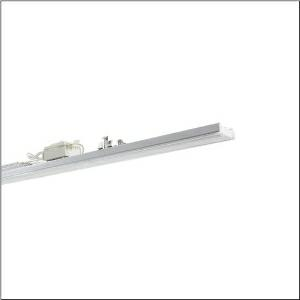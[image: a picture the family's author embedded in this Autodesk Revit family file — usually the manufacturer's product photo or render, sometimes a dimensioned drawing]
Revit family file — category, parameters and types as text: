
# Revit family: licross_r__11_recessed_mo_51te18dn495g_1a16
name_source: partatom
category: Lighting Fixtures
units: mm (PartAtom-declared; Revit-internal decimal feet)

## family parameters
Cut with Voids When Loaded = No
Host = Face
Light Source = No
Part Type = Normal
Room Calculation Point = No
Round Connector Dimension = Use Diameter
Shared = No

## types (1)
- --- (1 x LED, 9950 lm, 56.7 W, 4000K)
    Apparent Load = 57 VA
    CIE Flux Codes = 83 96 99 100 100
    Color Rendering = 80
    Color Temperature = 4000K
    Default Elevation = 1800 mm
    Description = Licross® 11 Recessed MO, luminaire insert, of sheet steel, galvanised, coil coated, white, length: 1.500mm, width: 66mm, height: 67mm, LED rated luminous flux: 9.950lm, light colour: 840, control gear: DALI 2, with plug, 5-pole, with phase selection, mains connection: 220..240V, AC, 50/60Hz, rated input power: 57W, halogen-free wiring, primary light control with lens, of plastic, primary optical cover: cover, of PMMA, light emission: direct distribution, primary light characteristic: symmetric, protection rating (complete): IP54, insulation class (complete): insulation class I (protective earthing), certification: CE, ENEC, VDE, UKCA, protection symbol: D if used in an environment with non-conductive dust loads with corresponding accessories, impact resistance: IK06, permissible ambient temperature for indoor applications: -25..+35°C, corresponds to IFS (International Featured Standards) requirements for safety and quality in the food industry, reducing of maximum allowable ambient temperature of 5°C with ceiling mounting, LABS conformity tested according to VDMA 24364:2018-05, packaging unit: 1 piece
    Height = 58 mm
    Lamp = 1 x LED
    Lamp Light Flux = 9950 lm
    Lamp Power = 56.7 W
    Lamp count = 1
    Length = 1500 mm
    Luminous efficacy = 175 lm/W
    Manufacturer = Siteco
    ModVariant = No
    Model = 51TE18DN495G
    Mounting Place = Ceiling
    Mounting Type = Pendant
    Number of Poles = 1
    OnlyDefault = Yes
    Power Factor = 1
    Product Name = Licross® 11 Recessed MO
    Product group = luminaire insert
    ProductGroupID = 902
    Protection Class = Protection class I
    Protection Degree = IP 54
    RLX_Detail_Level = 1
    RLX_Emergency_Light_Flux = 0 lm
    RLX_Emergency_Type = 0
    RLX_Emergency_Type_DB = No
    RlxData = <blob elided: 24441 chars, md5=ded6fcaa>
    Socket = socket
    Standby Power = 0 W
    System Light Flux = 9950 lm
    System Power = 57 W
    Type Comments = factory setting: luminous flux: 100 % | dim-lin: 254 | 378 mA
    Type Image = l_1296930.jpg
    URL = http://relux.com
    VarID = @adj_099072
    Voltage = 0 V
    Weight = 0.00 kg
    Width = 66 mm

## geometry (parser evidence)
native form markers: Blend x4, Sweep x10
no freeform markers — native parametric forms only
